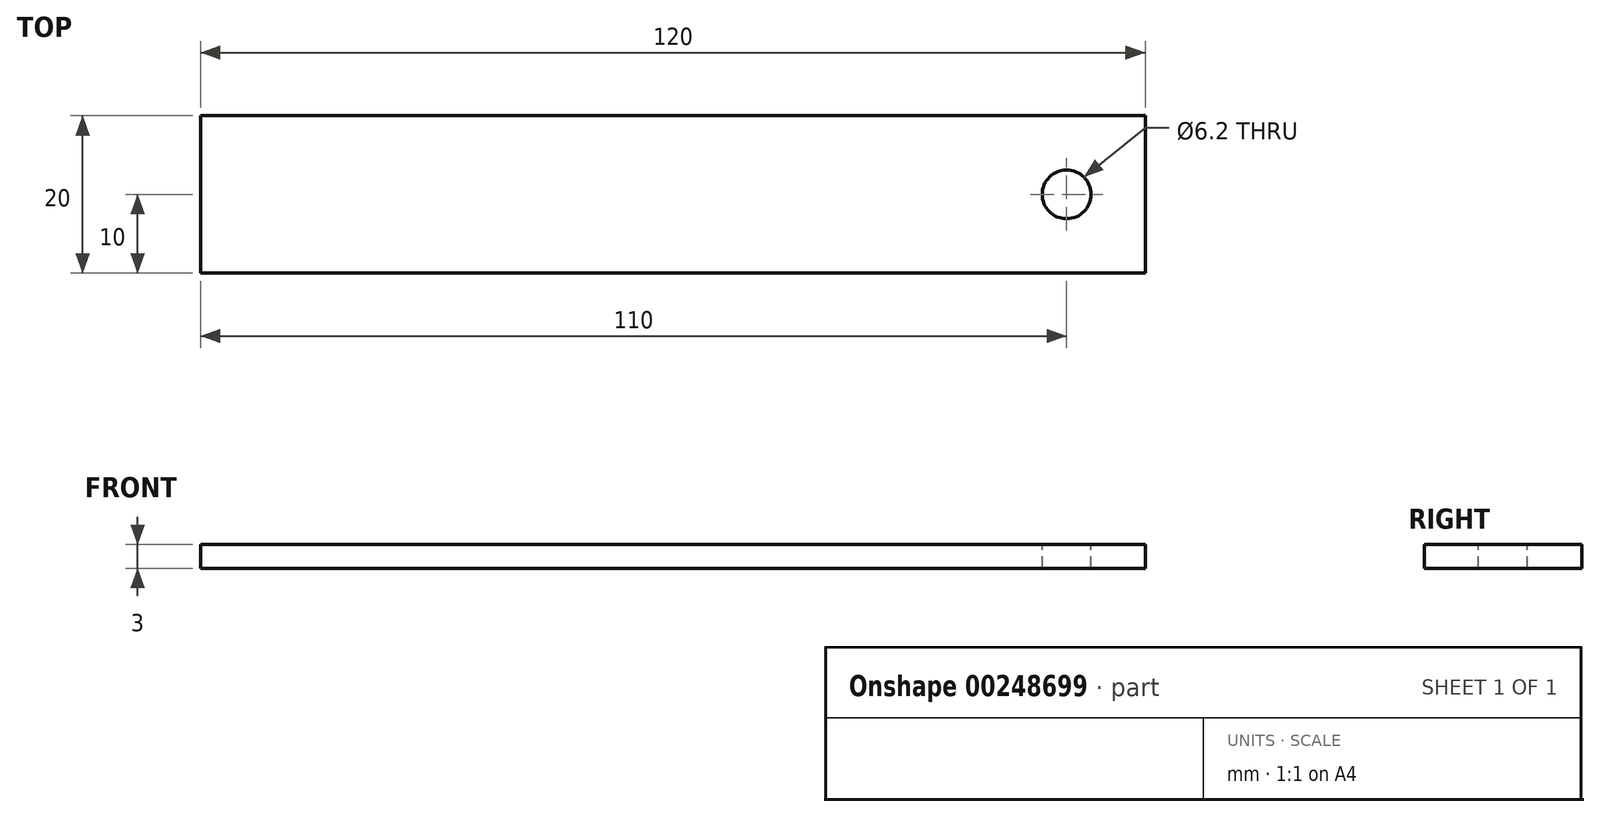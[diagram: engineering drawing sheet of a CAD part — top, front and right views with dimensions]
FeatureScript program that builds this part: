
annotation { "Feature Type Name" : "Feature", "Feature Type Description" : "" }
export const myFeature = defineFeature(function(context is Context, id is Id, definition is map)
    precondition{}
    {
        {
            var Q0;
            Q0=qCreatedBy(makeId("Top.planeOp"),FACE);
            var sketch = newSketch(context, id + "F0", { "sketchPlane" : qUnion([Q0])});
            skLineSegment(sketch, "E0.bottom", {"start": v(60, -10) * mm, "end": v(-60, -10) * mm});
            skLineSegment(sketch, "E0.top", {"start": v(60, 10) * mm, "end": v(-60, 10) * mm});
            skLineSegment(sketch, "E0.left", {"start": v(60, -10) * mm, "end": v(60, 10) * mm});
            skLineSegment(sketch, "E0.right", {"start": v(-60, -10) * mm, "end": v(-60, 10) * mm});
            skPoint(sketch, "E0.middle", {"position": v(0, 0) * mm});
            skSolve(sketch);
        }
        {
            var Q0;
            Q0=qSketchRegion(id+"F0",true);
            extrude(context, id + "F1", {"entities" : qUnion([Q0]), "depth" : 3 * mm});
        }
        {
            var Q0;
            Q0=makeQuery(id+"F1.opExtrude","CAP_FACE",FACE,{"disambiguationData":[OSD([sQuery(id+"F0.wireOp",EDGE,"E0.bottom"),sQuery(id+"F0.wireOp",EDGE,"E0.top"),sQuery(id+"F0.wireOp",EDGE,"E0.left"),sQuery(id+"F0.wireOp",EDGE,"E0.right")])],"isStart":false});
            var sketch = newSketch(context, id + "F2", { "sketchPlane" : qUnion([Q0])});
            skCircle(sketch, "E1", {"center": v(50, 0) * mm, "radius": 3.1 * mm});
            skPoint(sketch, "E1.centerSnap0", {"position": v(60, 0) * mm});
            skSolve(sketch);
        }
        {
            var Q0;
            Q0=qSketchRegion(id+"F2",true);
            extrude(context, id + "F3", {"entities" : qUnion([Q0]), "operationType" : NewBodyOperationType.REMOVE, "oppositeDirection" : true, "depth" : 25 * mm});
        }
    });
